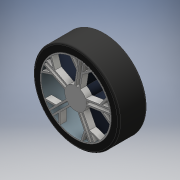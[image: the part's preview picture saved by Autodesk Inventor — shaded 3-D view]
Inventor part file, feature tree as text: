
AUTODESK INVENTOR PART (.ipt)
format: ipt  version: 2016 (Build 200138000, 138)  size: 417,792 bytes
history: native  units: mm
features: extrude x6, sketch x6, fillet x2, other x1
ambient origin geometry x8: Origin, YZ Plane, XZ Plane, XY Plane, X Axis, Y Axis, Z Axis, Center Point
bodies: Body1 (feature_tree)
feature tree (15):
  other  "Sólido1"
  extrude  "Extrusión1"  Depth=2.0mm TaperAngle=0.0deg
  extrude  "Extrusión5"  Depth=7.0mm TaperAngle=0.0deg
  extrude  "Extrusión6"  Depth=1.9mm TaperAngle=0.0deg
  extrude  "Extrusión7"  Depth=6.5mm
  extrude  "Extrusión8"  Depth=0.5mm
  fillet  "Empalme1"  Radius=0.5mm
  fillet  "Empalme2"  Radius=6.5mm
  extrude  "Extrusión9"  [1 undecoded]
  sketch  "Boceto1"  dims[d16=50.0mm d18=360.0deg d22=2.0mm d23=0.0mm]
  sketch  "Boceto7"  dims[d31=27.0mm d32=7.0mm d33=0.0mm]
  sketch  "Boceto8"  dims[d34=27.0mm d35=1.9mm d36=0.0mm]
  sketch  "Boceto9"  dims[d37=6.5mm d38=0.0mm d39=5.0mm]
  sketch  "Boceto10"  dims[d40=6.5mm d41=0.0mm d42=0.5mm d43=0.5mm d44=6.5mm d45=0.0mm]
  sketch  "Boceto11"
note: 1 required parameter value undecoded (feature->parameter linkage not recoverable at this tier; creation-order binding heuristic only, values carry confidence <= 0.55)
